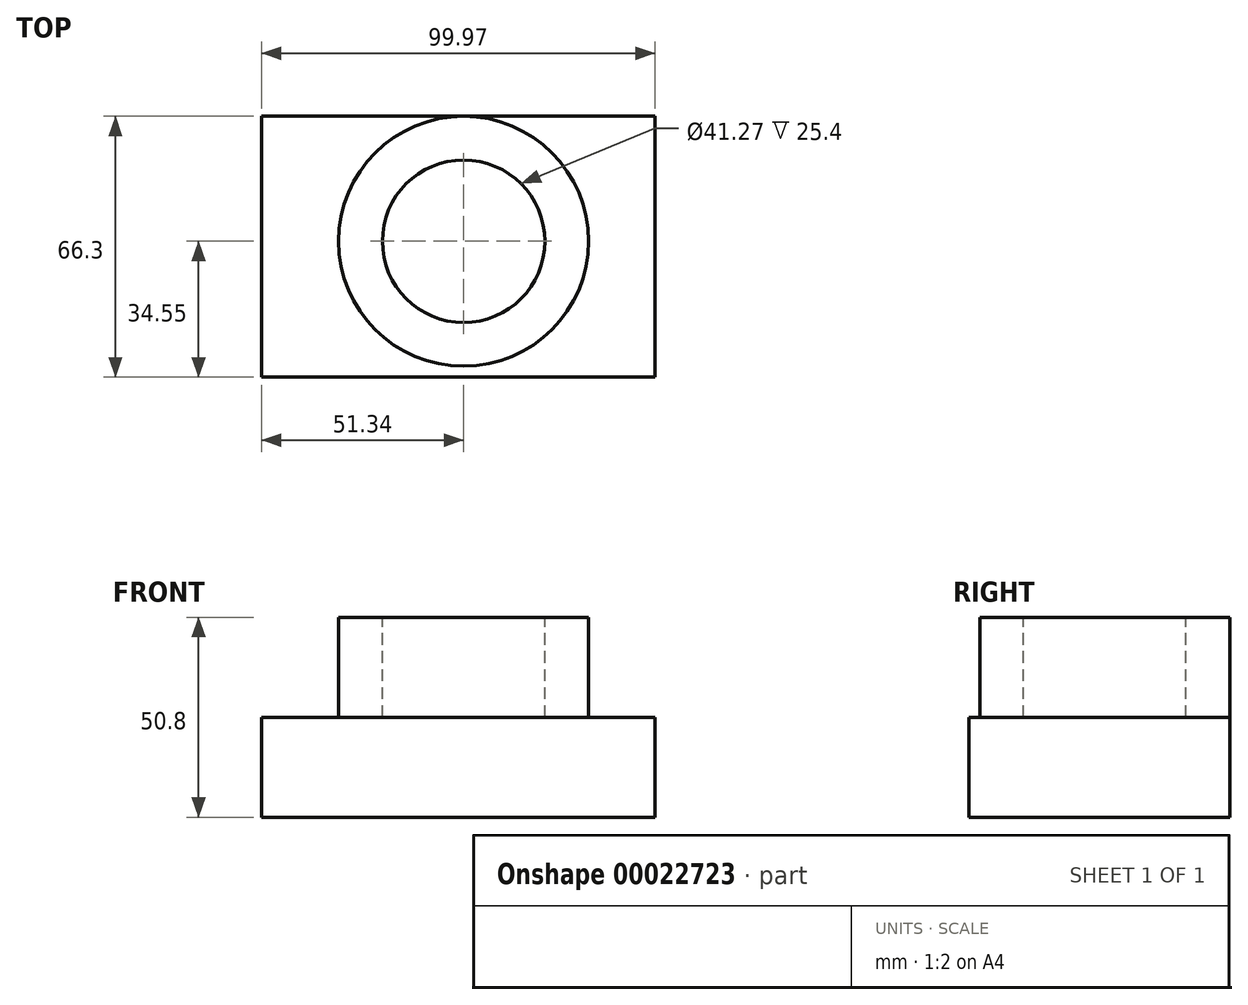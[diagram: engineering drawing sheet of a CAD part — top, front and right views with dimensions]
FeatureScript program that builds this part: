
annotation { "Feature Type Name" : "Feature", "Feature Type Description" : "" }
export const myFeature = defineFeature(function(context is Context, id is Id, definition is map)
    precondition{}
    {
        {
            var Q0;
            Q0=qCreatedBy(makeId("Top.planeOp"),FACE);
            var sketch = newSketch(context, id + "F0", { "sketchPlane" : qUnion([Q0])});
            skLineSegment(sketch, "E0.bottom", {"start": v(-51.34, 26.17) * mm, "end": v(48.63, 26.17) * mm});
            skLineSegment(sketch, "E0.top", {"start": v(-51.34, -40.13) * mm, "end": v(48.63, -40.13) * mm});
            skLineSegment(sketch, "E0.left", {"start": v(-51.34, 26.17) * mm, "end": v(-51.34, -40.13) * mm});
            skLineSegment(sketch, "E0.right", {"start": v(48.63, 26.17) * mm, "end": v(48.63, -40.13) * mm});
            skSolve(sketch);
        }
        {
            var Q0;
            Q0=makeQuery(id+"F0.imprint","IMPRINT",FACE,{"disambiguationData":[TD([[makeQuery(id+"F0.imprint","IMPRINT",EDGE,{"derivedFrom":sQuery(id+"F0.wireOp",EDGE,"E0.bottom")}),-1.0]])]});
            extrude(context, id + "F1", {"entities" : qUnion([Q0]), "depth" : 25.4 * mm});
        }
        {
            var Q0;
            Q0=makeQuery(id+"F1.opExtrude","CAP_FACE",FACE,{"disambiguationData":[OSD([sQuery(id+"F0.wireOp",EDGE,"E0.bottom"),sQuery(id+"F0.wireOp",EDGE,"E0.top"),sQuery(id+"F0.wireOp",EDGE,"E0.left"),sQuery(id+"F0.wireOp",EDGE,"E0.right")])],"isStart":false});
            var sketch = newSketch(context, id + "F2", { "sketchPlane" : qUnion([Q0])});
            skCircle(sketch, "E1", {"center": v(0, -5.58) * mm, "radius": 31.75 * mm});
            skSolve(sketch);
        }
        {
            var Q0;
            Q0=makeQuery(id+"F2.imprint","IMPRINT",FACE,{"disambiguationData":[TD([[makeQuery(id+"F2.imprint","IMPRINT",EDGE,{"derivedFrom":sQuery(id+"F2.wireOp",EDGE,"E1")}),1.0]])]});
            extrude(context, id + "F3", {"entities" : qUnion([Q0]), "operationType" : NewBodyOperationType.ADD, "depth" : 25.4 * mm});
        }
        {
            var Q0;
            Q0=makeQuery(id+"F3.opExtrude","CAP_FACE",FACE,{"disambiguationData":[OSD([sQuery(id+"F2.wireOp",EDGE,"E1")])],"isStart":false});
            var sketch = newSketch(context, id + "F4", { "sketchPlane" : qUnion([Q0])});
            skCircle(sketch, "E2", {"center": v(0, -5.58) * mm, "radius": 20.64 * mm});
            skSolve(sketch);
        }
        {
            var Q0;
            Q0=makeQuery(id+"F4.imprint","IMPRINT",FACE,{"disambiguationData":[TD([[makeQuery(id+"F4.imprint","IMPRINT",EDGE,{"derivedFrom":sQuery(id+"F4.wireOp",EDGE,"E2")}),1.0]])]});
            extrude(context, id + "F5", {"entities" : qUnion([Q0]), "operationType" : NewBodyOperationType.REMOVE, "oppositeDirection" : true, "depth" : 25.4 * mm});
        }
    });
